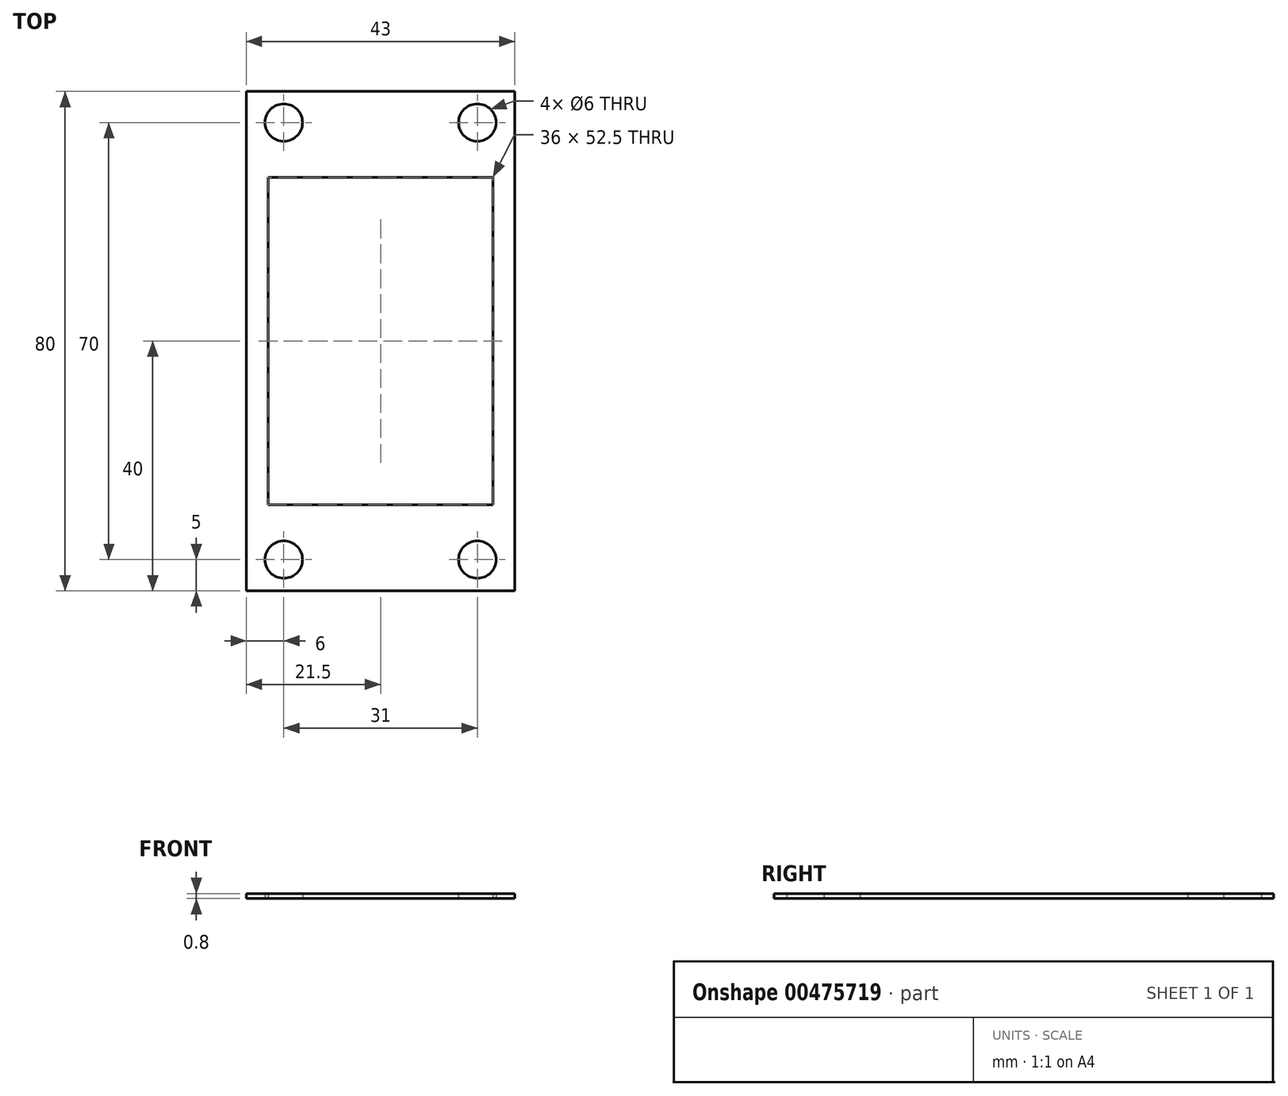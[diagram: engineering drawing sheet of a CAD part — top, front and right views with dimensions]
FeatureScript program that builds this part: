
annotation { "Feature Type Name" : "Feature", "Feature Type Description" : "" }
export const myFeature = defineFeature(function(context is Context, id is Id, definition is map)
    precondition{}
    {
        {
            var Q0;
            Q0=qCreatedBy(makeId("Top.planeOp"),FACE);
            var sketch = newSketch(context, id + "F0", { "sketchPlane" : qUnion([Q0])});
            skLineSegment(sketch, "E0.bottom", {"start": v(-19.1, 36.5) * mm, "end": v(23.9, 36.5) * mm});
            skLineSegment(sketch, "E0.top", {"start": v(-19.1, -43.5) * mm, "end": v(23.9, -43.5) * mm});
            skLineSegment(sketch, "E0.left", {"start": v(-19.1, 36.5) * mm, "end": v(-19.1, -43.5) * mm});
            skLineSegment(sketch, "E0.right", {"start": v(23.9, 36.5) * mm, "end": v(23.9, -43.5) * mm});
            skLineSegment(sketch, "E1.bottom", {"start": v(-15.6, 22.75) * mm, "end": v(20.4, 22.75) * mm});
            skLineSegment(sketch, "E1.top", {"start": v(-15.6, -29.75) * mm, "end": v(20.4, -29.75) * mm});
            skLineSegment(sketch, "E1.left", {"start": v(-15.6, 22.75) * mm, "end": v(-15.6, -29.75) * mm});
            skLineSegment(sketch, "E1.right", {"start": v(20.4, 22.75) * mm, "end": v(20.4, -29.75) * mm});
            skCircle(sketch, "E2", {"center": v(-13.1, 31.5) * mm, "radius": 3 * mm});
            skPoint(sketch, "E3", {"position": v(2.4, 22.75) * mm});
            skCircle(sketch, "E4.MirrorC", {"center": v(17.9, 31.5) * mm, "radius": 3 * mm});
            skPoint(sketch, "E5", {"position": v(-15.6, 22.75) * mm});
            skPoint(sketch, "E6", {"position": v(-15.6, -3.5) * mm});
            skCircle(sketch, "E7.MirrorC", {"center": v(17.9, -38.5) * mm, "radius": 3 * mm});
            skCircle(sketch, "E8.MirrorC", {"center": v(-13.1, -38.5) * mm, "radius": 3 * mm});
            skSolve(sketch);
        }
        {
            var Q0;
            Q0=makeQuery(id+"F0.imprint","IMPRINT",FACE,{"disambiguationData":[TD([[makeQuery(id+"F0.imprint","IMPRINT",EDGE,{"derivedFrom":sQuery(id+"F0.wireOp",EDGE,"E0.bottom")}),-1.0]])]});
            extrude(context, id + "F1", {"entities" : qUnion([Q0]), "depth" : 0.8 * mm});
        }
    });
